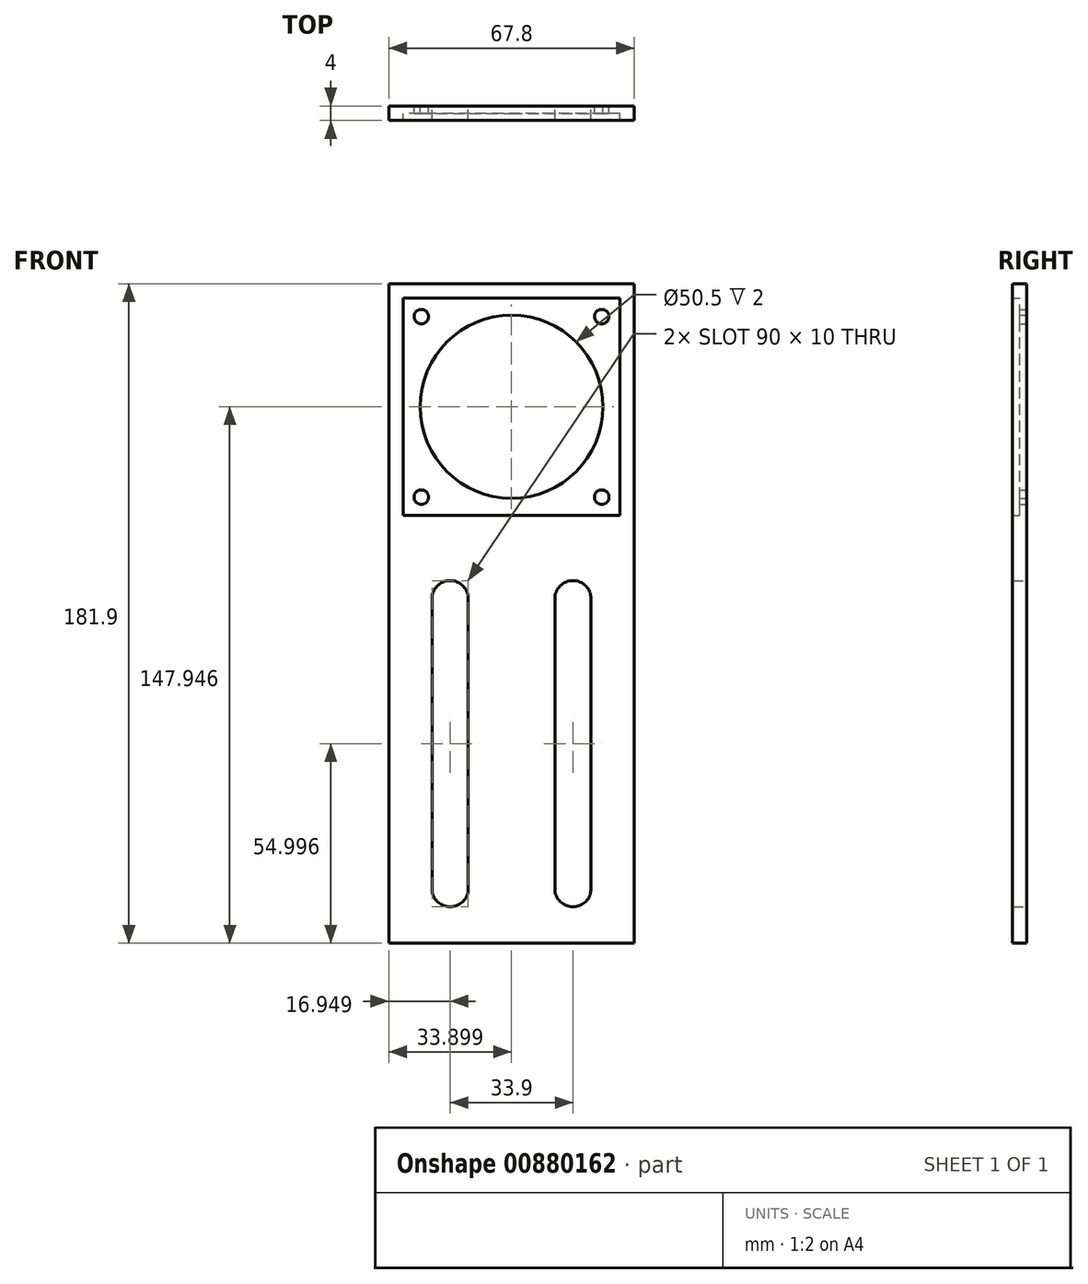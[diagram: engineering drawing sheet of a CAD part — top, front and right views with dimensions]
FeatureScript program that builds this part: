
annotation { "Feature Type Name" : "Feature", "Feature Type Description" : "" }
export const myFeature = defineFeature(function(context is Context, id is Id, definition is map)
    precondition{}
    {
        {
            var Q0;
            Q0=qCreatedBy(makeId("Front.planeOp"),FACE);
            var sketch = newSketch(context, id + "F0", { "sketchPlane" : qUnion([Q0])});
            skLineSegment(sketch, "E0.bottom", {"start": v(31.65, -24.62) * mm, "end": v(-28.15, -24.62) * mm});
            skLineSegment(sketch, "E0.top", {"start": v(31.65, 35.28) * mm, "end": v(-28.15, 35.28) * mm});
            skLineSegment(sketch, "E0.left", {"start": v(31.65, -24.62) * mm, "end": v(31.65, 35.28) * mm});
            skLineSegment(sketch, "E0.right", {"start": v(-28.15, -24.62) * mm, "end": v(-28.15, 35.28) * mm});
            skPoint(sketch, "E0.middle", {"position": v(1.75, 5.33) * mm});
            skLineSegment(sketch, "E1", {"start": v(-28.15, -24.62) * mm, "end": v(-32.15, -24.62) * mm});
            skLineSegment(sketch, "E2.0", {"start": v(-32.15, -28.62) * mm, "end": v(-32.15, 39.28) * mm});
            skLineSegment(sketch, "E2.1", {"start": v(35.65, -28.62) * mm, "end": v(-32.15, -28.62) * mm});
            skLineSegment(sketch, "E2.2", {"start": v(35.65, -28.62) * mm, "end": v(35.65, 39.28) * mm});
            skLineSegment(sketch, "E2.3", {"start": v(35.65, 39.28) * mm, "end": v(-32.15, 39.28) * mm});
            skLineSegment(sketch, "E3", {"start": v(-28.15, -24.62) * mm, "end": v(-23.15, -24.62) * mm});
            skLineSegment(sketch, "E4", {"start": v(-23.15, -24.62) * mm, "end": v(-23.15, -19.62) * mm});
            skCircle(sketch, "E5", {"center": v(-23.15, -19.62) * mm, "radius": 2 * mm});
            skCircle(sketch, "E6.0.1.0", {"center": v(-23.15, 30.18) * mm, "radius": 2 * mm});
            skCircle(sketch, "E6.1.0.0", {"center": v(26.65, -19.62) * mm, "radius": 2 * mm});
            skCircle(sketch, "E6.1.1.0", {"center": v(26.65, 30.18) * mm, "radius": 2 * mm});
            skLineSegment(sketch, "E6.direction1", {"start": v(-23.15, -19.62) * mm, "end": v(26.65, -19.62) * mm, "construction": true});
            skLineSegment(sketch, "E6.direction2", {"start": v(-23.15, -19.62) * mm, "end": v(-23.15, 30.18) * mm, "construction": true});
            skCircle(sketch, "E7", {"center": v(1.75, 5.33) * mm, "radius": 25.25 * mm});
            skLineSegment(sketch, "E8", {"start": v(-32.15, -28.62) * mm, "end": v(-32.15, -32.62) * mm});
            skLineSegment(sketch, "E9", {"start": v(-32.15, -32.62) * mm, "end": v(35.65, -32.62) * mm});
            skLineSegment(sketch, "E10", {"start": v(35.65, -32.62) * mm, "end": v(35.65, -28.62) * mm});
            skLineSegment(sketch, "E11", {"start": v(-32.15, -32.62) * mm, "end": v(-32.15, -142.62) * mm});
            skLineSegment(sketch, "E12", {"start": v(-32.15, -142.62) * mm, "end": v(35.65, -142.62) * mm});
            skLineSegment(sketch, "E13", {"start": v(35.65, -142.62) * mm, "end": v(35.65, -32.62) * mm});
            skLineSegment(sketch, "E14", {"start": v(-32.15, -142.62) * mm, "end": v(1.75, -142.62) * mm});
            skLineSegment(sketch, "E15", {"start": v(1.75, -142.62) * mm, "end": v(-15.2, -142.62) * mm});
            skLineSegment(sketch, "E16", {"start": v(35.65, -142.62) * mm, "end": v(18.7, -142.62) * mm});
            skLineSegment(sketch, "E17", {"start": v(18.7, -142.62) * mm, "end": v(18.7, -42.62) * mm});
            skLineSegment(sketch, "E18", {"start": v(18.7, -42.62) * mm, "end": v(-15.2, -42.62) * mm});
            skLineSegment(sketch, "E19", {"start": v(-15.2, -42.62) * mm, "end": v(-15.2, -142.62) * mm});
            skLineSegment(sketch, "E20", {"start": v(-15.2, -42.62) * mm, "end": v(-15.2, -47.62) * mm});
            skLineSegment(sketch, "E21", {"start": v(-15.2, -47.62) * mm, "end": v(18.7, -47.62) * mm});
            skLineSegment(sketch, "E22", {"start": v(-15.2, -142.62) * mm, "end": v(-15.2, -132.62) * mm});
            skLineSegment(sketch, "E23", {"start": v(-15.2, -132.62) * mm, "end": v(-15.2, -127.62) * mm});
            skLineSegment(sketch, "E24", {"start": v(-15.2, -127.62) * mm, "end": v(18.7, -127.62) * mm});
            skCircle(sketch, "E25", {"center": v(-15.2, -127.62) * mm, "radius": 5 * mm});
            skCircle(sketch, "E26", {"center": v(18.7, -127.62) * mm, "radius": 5 * mm});
            skCircle(sketch, "E27", {"center": v(-15.2, -47.62) * mm, "radius": 5 * mm});
            skCircle(sketch, "E28", {"center": v(18.7, -47.62) * mm, "radius": 5 * mm});
            skLineSegment(sketch, "E29", {"start": v(23.7, -47.62) * mm, "end": v(23.7, -127.62) * mm});
            skLineSegment(sketch, "E30", {"start": v(23.7, -127.62) * mm, "end": v(18.7, -127.62) * mm});
            skLineSegment(sketch, "E31", {"start": v(13.7, -127.62) * mm, "end": v(13.7, -47.62) * mm});
            skLineSegment(sketch, "E32", {"start": v(-10.2, -47.62) * mm, "end": v(-10.2, -127.62) * mm});
            skLineSegment(sketch, "E33", {"start": v(-20.2, -127.62) * mm, "end": v(-20.2, -47.62) * mm});
            skSolve(sketch);
        }
        {
            var Q0;
            Q0=makeQuery(id+"F0.imprint","IMPRINT",FACE,{"disambiguationData":[TD([[makeQuery(id+"F0.imprint","IMPRINT",EDGE,{"derivedFrom":sQuery(id+"F0.wireOp",EDGE,"E0.bottom")}),1.0]])]});
            var Q1;
            Q1=makeQuery(id+"F0.imprint","IMPRINT",FACE,{"disambiguationData":[TD([[makeQuery(id+"F0.imprint","IMPRINT",EDGE,{"derivedFrom":sQuery(id+"F0.wireOp",EDGE,"E2.1")}),1.0]])]});
            extrude(context, id + "F1", {"entities" : qUnion([Q0, Q1]), "depth" : 4 * mm, "offsetDistance" : 25 * mm});
        }
        {
            var Q0;
            Q0 = qSketchRegion(id + "F0", true);
            var Q1;
            {var subQ0=sQuery(id+"F0.wireOp",EDGE,"E31");Q1=makeQuery(id+"F0.imprint","IMPRINT",FACE,{"disambiguationData":[TD([[makeQuery(id+"F0.imprint","IMPRINT",EDGE,{"derivedFrom":subQ0}),1.0]])]});}
            var Q2;
            {var subQ0=sQuery(id+"F0.wireOp",EDGE,"E18");Q2=makeQuery(id+"F0.imprint","IMPRINT",FACE,{"disambiguationData":[TD([[makeQuery(id+"F0.imprint","IMPRINT",EDGE,{"derivedFrom":subQ0}),1.0]])]});}
            extrude(context, id + "F2", {"entities" : qUnion([Q0, Q1, Q2]), "operationType" : NewBodyOperationType.ADD, "depth" : 4 * mm, "offsetDistance" : 25 * mm});
        }
        {
            var Q0;
            Q0=makeQuery(id+"F0.imprint","IMPRINT",FACE,{"disambiguationData":[TD([[makeQuery(id+"F0.imprint","IMPRINT",EDGE,{"derivedFrom":sQuery(id+"F0.wireOp",EDGE,"E0.bottom")}),-1.0]])]});
            extrude(context, id + "F3", {"entities" : qUnion([Q0]), "operationType" : NewBodyOperationType.ADD, "depth" : 2 * mm, "offsetDistance" : 25 * mm});
        }
    });
